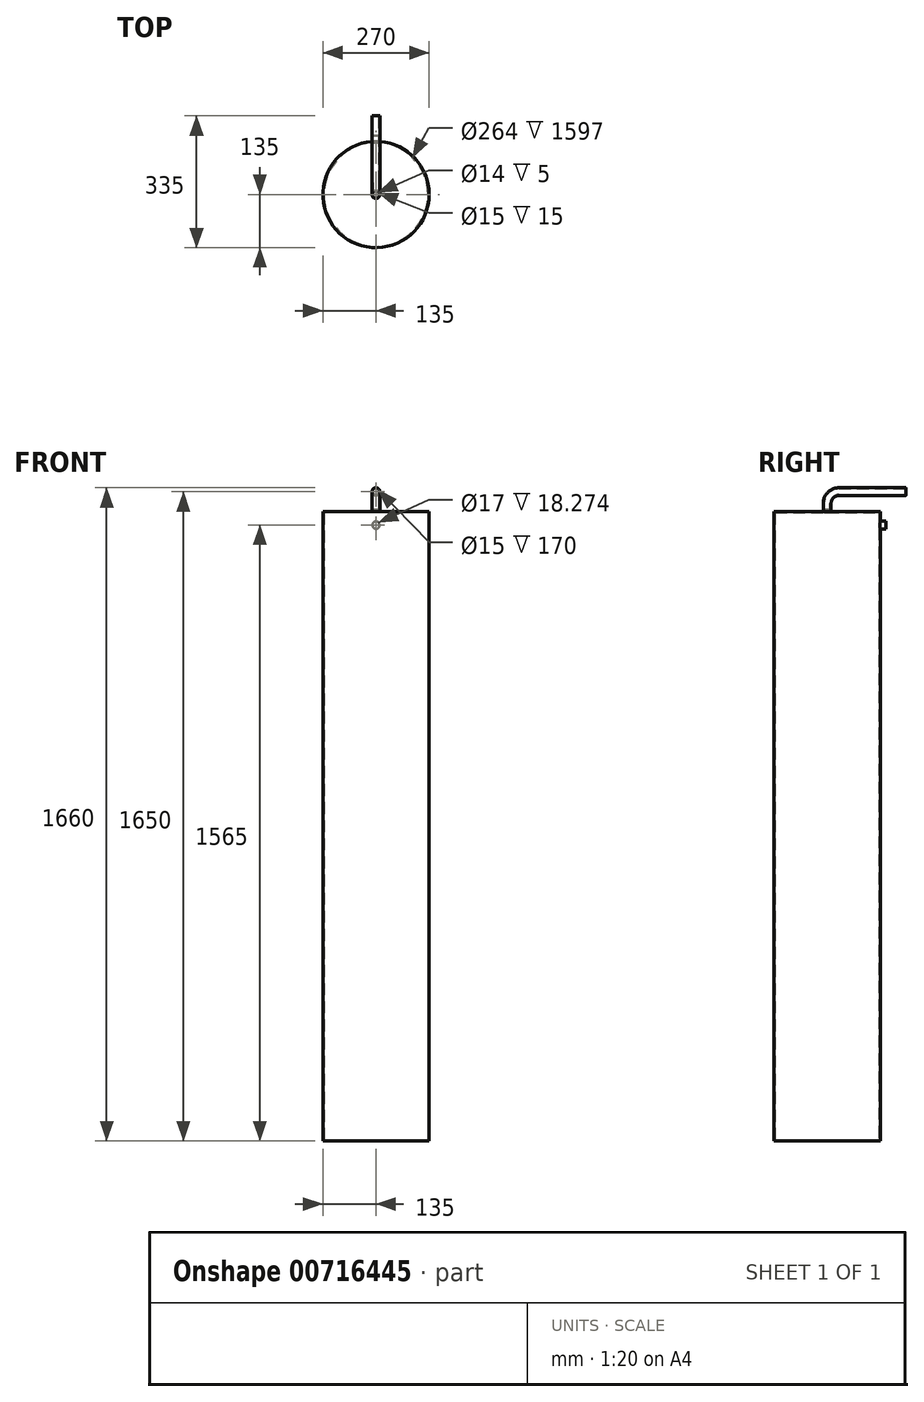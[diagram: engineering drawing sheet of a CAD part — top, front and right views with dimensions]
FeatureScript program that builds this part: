
annotation { "Feature Type Name" : "Feature", "Feature Type Description" : "" }
export const myFeature = defineFeature(function(context is Context, id is Id, definition is map)
    precondition{}
    {
        {
            var Q0;
            Q0=qCreatedBy(makeId("Top.planeOp"),FACE);
            var sketch = newSketch(context, id + "F0", { "sketchPlane" : qUnion([Q0])});
            skCircle(sketch, "E0", {"center": v(0, 0) * mm, "radius": 135 * mm});
            skSolve(sketch);
        }
        {
            var Q0;
            Q0 = qSketchRegion(id + "F0", true);
            extrude(context, id + "F1", {"entities" : qUnion([Q0]), "depth" : 1600 * mm, "offsetDistance" : 25 * mm});
        }
        {
            var Q0;
            Q0=makeQuery(id+"F1.opExtrude","CAP_FACE",FACE,{"disambiguationData":[OSD([sQuery(id+"F0.wireOp",EDGE,"E0")])],"isStart":false});
            var sketch = newSketch(context, id + "F2", { "sketchPlane" : qUnion([Q0])});
            skCircle(sketch, "E1", {"center": v(0, 0) * mm, "radius": 10 * mm});
            skSolve(sketch);
        }
        {
            var Q0;
            Q0=qCreatedBy(makeId("Right.planeOp"),FACE);
            var sketch = newSketch(context, id + "F3", { "sketchPlane" : qUnion([Q0])});
            skLineSegment(sketch, "E2", {"start": v(0, 1600) * mm, "end": v(0, 1620) * mm});
            skLineSegment(sketch, "E3", {"start": v(30, 1650) * mm, "end": v(200, 1650) * mm});
            skPoint(sketch, "E4.visualSharp", {"position": v(0, 1650) * mm});
            skArc(sketch, "E4.filletArc", {"start": v(30, 1650) * mm, "mid": v(8.79, 1641.21) * mm, "end": v(0, 1620) * mm});
            skSolve(sketch);
        }
        {
            var Q0;
            Q0=qCreatedBy(makeId("Front.planeOp"),FACE);
            cPlane(context, id + "F4", {"entities" : qUnion([Q0]), "cplaneType" : CPlaneType.OFFSET, "offset" : 125 * mm, "oppositeDirection" : true, "width" : 150 * mm, "height" : 150 * mm});
        }
        {
            var Q0;
            Q0=qCreatedBy(id+"F4.planeOp",FACE);
            var sketch = newSketch(context, id + "F5", { "sketchPlane" : qUnion([Q0])});
            skCircle(sketch, "E5", {"center": v(0, 1565) * mm, "radius": 10 * mm});
            skSolve(sketch);
        }
        {
            var Q0;
            Q0 = qSketchRegion(id + "F2", true);
            extrude(context, id + "F6", {"entities" : qUnion([Q0]), "operationType" : NewBodyOperationType.ADD, "depth" : 5 * mm, "offsetDistance" : 25 * mm});
        }
        {
            var Q0;
            Q0 = qSketchRegion(id + "F5", true);
            extrude(context, id + "F7", {"entities" : qUnion([Q0]), "operationType" : NewBodyOperationType.ADD, "oppositeDirection" : true, "depth" : 25 * mm, "offsetDistance" : 25 * mm});
        }
        {
            var Q0;
            Q0=makeQuery(id+"F1.opExtrude","CAP_FACE",FACE,{"disambiguationData":[OSD([sQuery(id+"F0.wireOp",EDGE,"E0")])],"isStart":true});
            shell(context, id + "F8", {"entities" : qUnion([Q0]), "thickness" : 3 * mm});
        }
        {
            var Q0;
            Q0=makeQuery(id+"F7.opExtrude","CAP_FACE",FACE,{"disambiguationData":[OSD([sQuery(id+"F5.wireOp",EDGE,"E5")])],"isStart":false});
            var sketch = newSketch(context, id + "F9", { "sketchPlane" : qUnion([Q0])});
            skCircle(sketch, "E6", {"center": v(0, 1565) * mm, "radius": 8.5 * mm});
            skSolve(sketch);
        }
        {
            var Q0;
            Q0 = qSketchRegion(id + "F9", true);
            extrude(context, id + "F10", {"entities" : qUnion([Q0]), "operationType" : NewBodyOperationType.REMOVE, "oppositeDirection" : true, "depth" : 50 * mm, "offsetDistance" : 25 * mm});
        }
        {
            var Q0;
            Q0=makeQuery(id+"F6.opExtrude","CAP_FACE",FACE,{"disambiguationData":[OSD([sQuery(id+"F2.wireOp",EDGE,"E1")])],"isStart":false});
            var sketch = newSketch(context, id + "F11", { "sketchPlane" : qUnion([Q0])});
            skCircle(sketch, "E7", {"center": v(0, 0) * mm, "radius": 10 * mm});
            skCircle(sketch, "E8", {"center": v(0, 0) * mm, "radius": 7.5 * mm});
            skSolve(sketch);
        }
        {
            var Q0;
            Q0=makeQuery(id+"F11.imprint","IMPRINT",FACE,{"disambiguationData":[TD([[makeQuery(id+"F11.imprint","IMPRINT",EDGE,{"derivedFrom":sQuery(id+"F11.wireOp",EDGE,"E7")}),1.0]])]});
            var Q1;
            Q1 = qConstructionFilter(qBodyType(qCreatedBy(id + "F3" ,EDGE), BodyType.WIRE), ConstructionObject.NO);
            sweep(context, id + "F12", {"operationType" : NewBodyOperationType.ADD, "profiles" : qUnion([Q0]), "path" : qUnion([Q1])});
        }
    });
